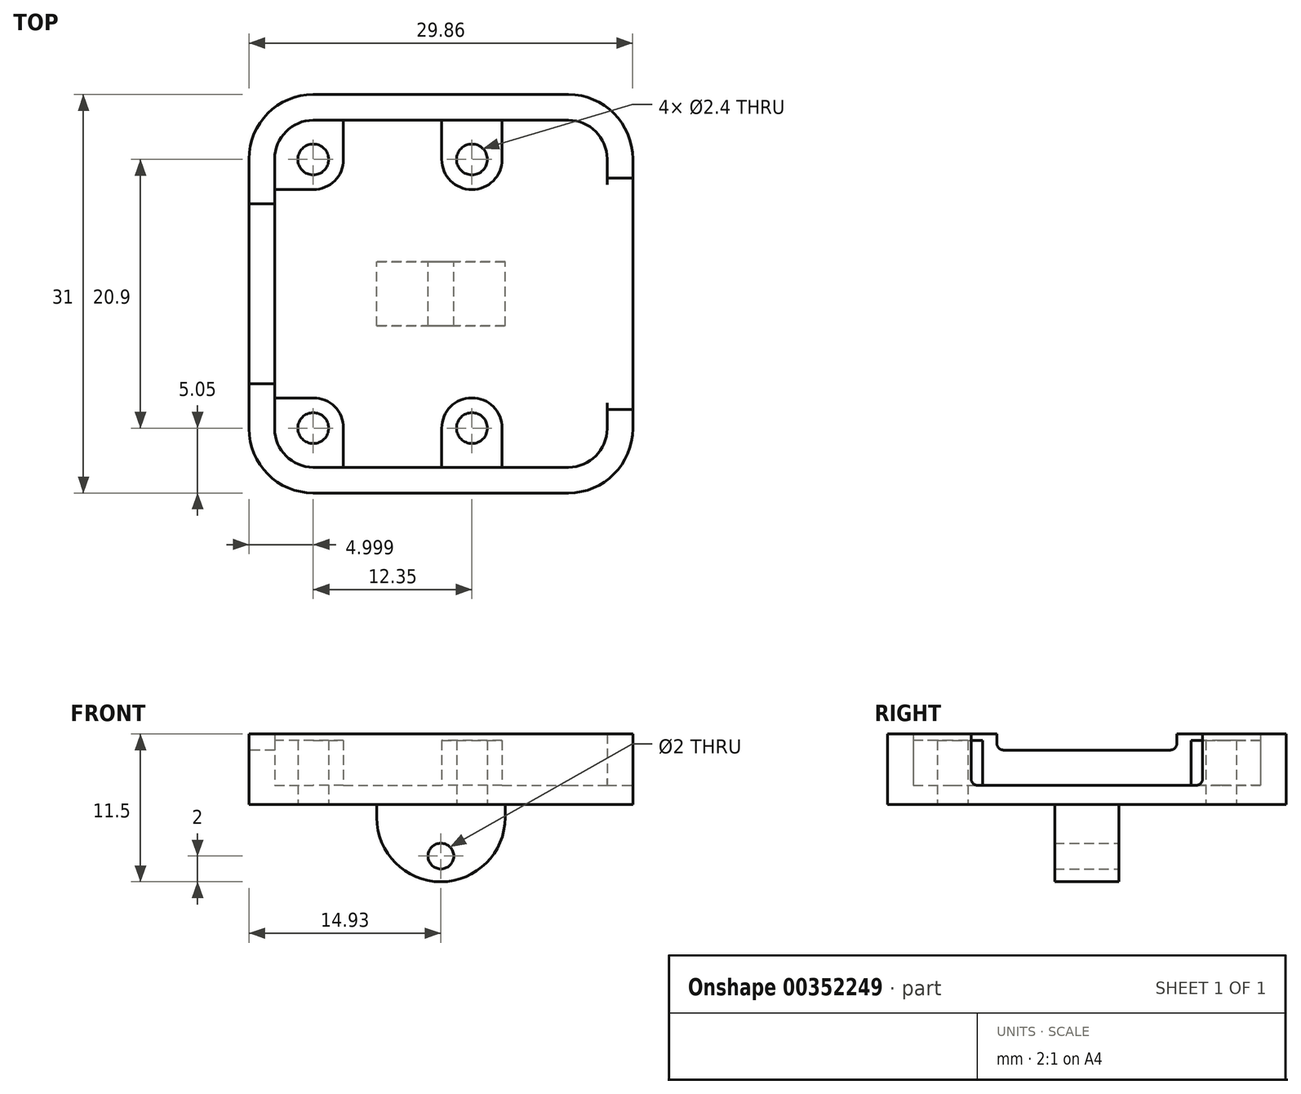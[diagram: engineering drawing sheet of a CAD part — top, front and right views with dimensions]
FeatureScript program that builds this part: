
annotation { "Feature Type Name" : "Feature", "Feature Type Description" : "" }
export const myFeature = defineFeature(function(context is Context, id is Id, definition is map)
    precondition{}
    {
        {
            var Q0;
            Q0=qCreatedBy(makeId("Top.planeOp"),FACE);
            var sketch = newSketch(context, id + "F0", { "sketchPlane" : qUnion([Q0])});
            skPoint(sketch, "E0.middle", {"position": v(0, 0) * mm});
            skPoint(sketch, "E1.visualSharp", {"position": v(-11.93, 12.5) * mm});
            skPoint(sketch, "E2.visualSharp", {"position": v(-11.93, -12.5) * mm});
            skPoint(sketch, "E3.visualSharp", {"position": v(11.93, 12.5) * mm});
            skPoint(sketch, "E4.visualSharp", {"position": v(11.93, -12.5) * mm});
            skLineSegment(sketch, "E5", {"start": v(-9.93, 14.98) * mm, "end": v(-9.93, -15.05) * mm, "construction": true});
            skLineSegment(sketch, "E6", {"start": v(-20.4, -10.45) * mm, "end": v(21.47, -10.45) * mm, "construction": true});
            skLineSegment(sketch, "E7", {"start": v(-14.71, 10.45) * mm, "end": v(19.25, 10.45) * mm, "construction": true});
            skCircle(sketch, "E8", {"center": v(-9.93, 10.45) * mm, "radius": 1.2 * mm});
            skCircle(sketch, "E9", {"center": v(-9.93, -10.45) * mm, "radius": 1.2 * mm});
            skLineSegment(sketch, "E10", {"start": v(2.42, 14.76) * mm, "end": v(2.42, -15.1) * mm, "construction": true});
            skCircle(sketch, "E11", {"center": v(2.42, 10.45) * mm, "radius": 1.2 * mm});
            skCircle(sketch, "E12", {"center": v(2.42, -10.45) * mm, "radius": 1.2 * mm});
            skLineSegment(sketch, "E13", {"start": v(2.47, 15.16) * mm, "end": v(2.47, -14.75) * mm, "construction": true});
            skPoint(sketch, "E14.middle", {"position": v(2.47, 0) * mm});
            skCircle(sketch, "E15", {"center": v(-9.93, 10.45) * mm, "radius": 2.35 * mm});
            skCircle(sketch, "E16", {"center": v(-9.93, -10.45) * mm, "radius": 2.35 * mm});
            skCircle(sketch, "E17", {"center": v(2.42, -10.45) * mm, "radius": 2.35 * mm});
            skCircle(sketch, "E18", {"center": v(2.42, 10.45) * mm, "radius": 2.35 * mm});
            skLineSegment(sketch, "E19.0", {"start": v(9.93, 13.5) * mm, "end": v(-9.93, 13.5) * mm});
            skArc(sketch, "E19.1", {"start": v(12.93, 10.5) * mm, "mid": v(12.05, 12.62) * mm, "end": v(9.93, 13.5) * mm});
            skArc(sketch, "E19.2", {"start": v(-9.93, 13.5) * mm, "mid": v(-12.05, 12.62) * mm, "end": v(-12.93, 10.5) * mm});
            skLineSegment(sketch, "E19.3", {"start": v(12.93, 10.5) * mm, "end": v(12.93, -10.5) * mm});
            skLineSegment(sketch, "E19.4", {"start": v(-12.93, 10.5) * mm, "end": v(-12.93, -10.5) * mm});
            skArc(sketch, "E19.5", {"start": v(-12.93, -10.5) * mm, "mid": v(-12.05, -12.62) * mm, "end": v(-9.93, -13.5) * mm});
            skLineSegment(sketch, "E19.6", {"start": v(9.93, -13.5) * mm, "end": v(-9.93, -13.5) * mm});
            skArc(sketch, "E19.7", {"start": v(9.93, -13.5) * mm, "mid": v(12.05, -12.62) * mm, "end": v(12.93, -10.5) * mm});
            skArc(sketch, "E20.0", {"start": v(14.93, 10.5) * mm, "mid": v(13.47, 14.04) * mm, "end": v(9.93, 15.5) * mm});
            skLineSegment(sketch, "E20.1", {"start": v(14.93, 10.5) * mm, "end": v(14.93, -10.5) * mm});
            skLineSegment(sketch, "E20.2", {"start": v(9.93, 15.5) * mm, "end": v(-9.93, 15.5) * mm});
            skArc(sketch, "E20.3", {"start": v(9.93, -15.5) * mm, "mid": v(13.47, -14.04) * mm, "end": v(14.93, -10.5) * mm});
            skArc(sketch, "E20.4", {"start": v(-9.93, 15.5) * mm, "mid": v(-13.47, 14.04) * mm, "end": v(-14.93, 10.5) * mm});
            skLineSegment(sketch, "E20.5", {"start": v(-14.93, 10.5) * mm, "end": v(-14.93, -10.5) * mm});
            skArc(sketch, "E20.6", {"start": v(-14.93, -10.5) * mm, "mid": v(-13.47, -14.04) * mm, "end": v(-9.93, -15.5) * mm});
            skLineSegment(sketch, "E20.7", {"start": v(9.93, -15.5) * mm, "end": v(-9.93, -15.5) * mm});
            skLineSegment(sketch, "E21", {"start": v(-9.93, 8.1) * mm, "end": v(-12.93, 8.1) * mm});
            skLineSegment(sketch, "E22", {"start": v(-7.58, 10.45) * mm, "end": v(-7.58, 13.5) * mm});
            skLineSegment(sketch, "E23", {"start": v(0.07, 10.45) * mm, "end": v(0.07, 13.5) * mm});
            skLineSegment(sketch, "E24", {"start": v(4.77, 10.45) * mm, "end": v(4.77, 13.5) * mm});
            skLineSegment(sketch, "E25", {"start": v(0.07, -10.45) * mm, "end": v(0.07, -13.5) * mm});
            skLineSegment(sketch, "E26", {"start": v(4.77, -10.45) * mm, "end": v(4.77, -13.5) * mm});
            skLineSegment(sketch, "E27", {"start": v(-9.93, -8.1) * mm, "end": v(-12.93, -8.1) * mm});
            skLineSegment(sketch, "E28", {"start": v(-7.58, -10.45) * mm, "end": v(-7.58, -13.5) * mm});
            skSolve(sketch);
        }
        {
            var Q0;
            Q0=makeQuery(id+"F0.imprint","IMPRINT",FACE,{"disambiguationData":[TD([[makeQuery(id+"F0.imprint","IMPRINT",EDGE,{"derivedFrom":sQuery(id+"F0.wireOp",EDGE,"E19.0")}),-1.0]])]});
            var Q1;
            Q1=makeQuery(id+"F0.imprint","IMPRINT",FACE,{"disambiguationData":[TD([[makeQuery(id+"F0.imprint","IMPRINT",EDGE,{"derivedFrom":sQuery(id+"F0.wireOp",EDGE,"E0.left")}),-1.0]])]});
            var Q2;
            Q2=makeQuery(id+"F0.imprint","IMPRINT",FACE,{"disambiguationData":[TD([[makeQuery(id+"F0.imprint","IMPRINT",EDGE,{"derivedFrom":sQuery(id+"F0.wireOp",EDGE,"E12")}),-1.0]])]});
            var Q3;
            {var subQ0=sQuery(id+"F0.wireOp",EDGE,"E2.filletArc");Q3=makeQuery(id+"F0.imprint","IMPRINT",FACE,{"disambiguationData":[TD([[makeQuery(id+"F0.imprint","IMPRINT",EDGE,{"derivedFrom":subQ0}),1.0]])]});}
            var Q4;
            Q4=makeQuery(id+"F0.imprint","IMPRINT",FACE,{"disambiguationData":[TD([[makeQuery(id+"F0.imprint","IMPRINT",EDGE,{"derivedFrom":sQuery(id+"F0.wireOp",EDGE,"E0.left")}),1.0]])]});
            var Q5;
            {var subQ0=sQuery(id+"F0.wireOp",EDGE,"E1.filletArc");Q5=makeQuery(id+"F0.imprint","IMPRINT",FACE,{"disambiguationData":[TD([[makeQuery(id+"F0.imprint","IMPRINT",EDGE,{"derivedFrom":subQ0}),1.0]])]});}
            var Q6;
            Q6=makeQuery(id+"F0.imprint","IMPRINT",FACE,{"disambiguationData":[TD([[makeQuery(id+"F0.imprint","IMPRINT",EDGE,{"derivedFrom":sQuery(id+"F0.wireOp",EDGE,"E11")}),-1.0]])]});
            var Q7;
            {var subQ0=sQuery(id+"F0.wireOp",EDGE,"E18");var subQ1=sQuery(id+"F0.wireOp",EDGE,"E0.bottom");var subQ2=makeQuery(id+"F0.imprint","INTERSECT",VERTEX,{"disambiguationData":[OD(0.0)],"derivedFrom":[subQ1,subQ0]});Q7=makeQuery(id+"F0.imprint","IMPRINT",FACE,{"disambiguationData":[TD([[makeQuery(id+"F0.imprint","IMPRINT",EDGE,{"disambiguationData":[TD([[subQ2,-1.0]])],"derivedFrom":subQ1}),-1.0]])]});}
            var Q8;
            {var subQ0=sQuery(id+"F0.wireOp",EDGE,"E1.filletArc");Q8=makeQuery(id+"F0.imprint","IMPRINT",FACE,{"disambiguationData":[TD([[makeQuery(id+"F0.imprint","IMPRINT",EDGE,{"derivedFrom":subQ0}),-1.0]])]});}
            var Q9;
            {var subQ0=sQuery(id+"F0.wireOp",EDGE,"E2.filletArc");Q9=makeQuery(id+"F0.imprint","IMPRINT",FACE,{"disambiguationData":[TD([[makeQuery(id+"F0.imprint","IMPRINT",EDGE,{"derivedFrom":subQ0}),-1.0]])]});}
            var Q10;
            {var subQ0=sQuery(id+"F0.wireOp",EDGE,"E17");var subQ1=sQuery(id+"F0.wireOp",EDGE,"E0.top");var subQ2=makeQuery(id+"F0.imprint","INTERSECT",VERTEX,{"disambiguationData":[OD(0.0)],"derivedFrom":[subQ1,subQ0]});Q10=makeQuery(id+"F0.imprint","IMPRINT",FACE,{"disambiguationData":[TD([[makeQuery(id+"F0.imprint","IMPRINT",EDGE,{"disambiguationData":[TD([[subQ2,-1.0]])],"derivedFrom":subQ1}),1.0]])]});}
            var Q11;
            {var subQ0=sQuery(id+"F0.wireOp",EDGE,"E19.2");Q11=makeQuery(id+"F0.imprint","IMPRINT",FACE,{"disambiguationData":[TD([[makeQuery(id+"F0.imprint","IMPRINT",EDGE,{"derivedFrom":subQ0}),1.0]])]});}
            var Q12;
            {var subQ0=sQuery(id+"F0.wireOp",EDGE,"E21");var subQ1=sQuery(id+"F0.wireOp",EDGE,"E0.right");var subQ2=makeQuery(id+"F0.imprint","INTERSECT",VERTEX,{"derivedFrom":[subQ1,subQ0]});Q12=makeQuery(id+"F0.imprint","IMPRINT",FACE,{"disambiguationData":[TD([[makeQuery(id+"F0.imprint","IMPRINT",EDGE,{"disambiguationData":[TD([[subQ2,-1.0]])],"derivedFrom":subQ1}),-1.0]])]});}
            var Q13;
            {var subQ0=sQuery(id+"F0.wireOp",EDGE,"E19.5");Q13=makeQuery(id+"F0.imprint","IMPRINT",FACE,{"disambiguationData":[TD([[makeQuery(id+"F0.imprint","IMPRINT",EDGE,{"derivedFrom":subQ0}),1.0]])]});}
            var Q14;
            {var subQ0=sQuery(id+"F0.wireOp",EDGE,"E27");var subQ1=sQuery(id+"F0.wireOp",EDGE,"E0.right");var subQ2=makeQuery(id+"F0.imprint","INTERSECT",VERTEX,{"derivedFrom":[subQ1,subQ0]});Q14=makeQuery(id+"F0.imprint","IMPRINT",FACE,{"disambiguationData":[TD([[makeQuery(id+"F0.imprint","IMPRINT",EDGE,{"disambiguationData":[TD([[subQ2,-1.0]])],"derivedFrom":subQ1}),1.0]])]});}
            var Q15;
            {var subQ0=sQuery(id+"F0.wireOp",EDGE,"E28");var subQ1=sQuery(id+"F0.wireOp",EDGE,"E0.top");var subQ2=makeQuery(id+"F0.imprint","INTERSECT",VERTEX,{"derivedFrom":[subQ1,subQ0]});Q15=makeQuery(id+"F0.imprint","IMPRINT",FACE,{"disambiguationData":[TD([[makeQuery(id+"F0.imprint","IMPRINT",EDGE,{"disambiguationData":[TD([[subQ2,-1.0]])],"derivedFrom":subQ1}),-1.0]])]});}
            var Q16;
            {var subQ0=sQuery(id+"F0.wireOp",EDGE,"E25");var subQ1=sQuery(id+"F0.wireOp",EDGE,"E0.top");var subQ2=makeQuery(id+"F0.imprint","INTERSECT",VERTEX,{"derivedFrom":[subQ1,subQ0]});Q16=makeQuery(id+"F0.imprint","IMPRINT",FACE,{"disambiguationData":[TD([[makeQuery(id+"F0.imprint","IMPRINT",EDGE,{"disambiguationData":[TD([[subQ2,-1.0]])],"derivedFrom":subQ1}),1.0]])]});}
            var Q17;
            {var subQ3=sQuery(id+"F0.wireOp",EDGE,"E26");var subQ6=sQuery(id+"F0.wireOp",EDGE,"E0.top");var subQ10=makeQuery(id+"F0.imprint","INTERSECT",VERTEX,{"derivedFrom":[subQ6,subQ3]});Q17=makeQuery(id+"F0.imprint","IMPRINT",FACE,{"disambiguationData":[TD([[makeQuery(id+"F0.imprint","IMPRINT",EDGE,{"disambiguationData":[TD([[subQ10,-1.0]])],"derivedFrom":subQ6}),1.0]])]});}
            var Q18;
            {var subQ0=sQuery(id+"F0.wireOp",EDGE,"E26");var subQ1=sQuery(id+"F0.wireOp",EDGE,"E0.top");var subQ2=makeQuery(id+"F0.imprint","INTERSECT",VERTEX,{"derivedFrom":[subQ1,subQ0]});Q18=makeQuery(id+"F0.imprint","IMPRINT",FACE,{"disambiguationData":[TD([[makeQuery(id+"F0.imprint","IMPRINT",EDGE,{"disambiguationData":[TD([[subQ2,-1.0]])],"derivedFrom":subQ1}),-1.0]])]});}
            var Q19;
            {var subQ0=sQuery(id+"F0.wireOp",EDGE,"E17");var subQ1=sQuery(id+"F0.wireOp",EDGE,"E0.top");var subQ2=makeQuery(id+"F0.imprint","INTERSECT",VERTEX,{"disambiguationData":[OD(1.0)],"derivedFrom":[subQ1,subQ0]});Q19=makeQuery(id+"F0.imprint","IMPRINT",FACE,{"disambiguationData":[TD([[makeQuery(id+"F0.imprint","IMPRINT",EDGE,{"disambiguationData":[TD([[subQ2,-1.0]])],"derivedFrom":subQ1}),-1.0]])]});}
            var Q20;
            {var subQ0=sQuery(id+"F0.wireOp",EDGE,"E22");var subQ1=sQuery(id+"F0.wireOp",EDGE,"E0.bottom");var subQ2=makeQuery(id+"F0.imprint","INTERSECT",VERTEX,{"derivedFrom":[subQ1,subQ0]});Q20=makeQuery(id+"F0.imprint","IMPRINT",FACE,{"disambiguationData":[TD([[makeQuery(id+"F0.imprint","IMPRINT",EDGE,{"disambiguationData":[TD([[subQ2,-1.0]])],"derivedFrom":subQ1}),1.0]])]});}
            var Q21;
            {var subQ0=sQuery(id+"F0.wireOp",EDGE,"E15");var subQ1=sQuery(id+"F0.wireOp",EDGE,"E0.right");var subQ2=makeQuery(id+"F0.imprint","INTERSECT",VERTEX,{"derivedFrom":[subQ1,subQ0]});Q21=makeQuery(id+"F0.imprint","IMPRINT",FACE,{"disambiguationData":[TD([[makeQuery(id+"F0.imprint","IMPRINT",EDGE,{"disambiguationData":[TD([[subQ2,-1.0]])],"derivedFrom":subQ1}),1.0]])]});}
            var Q22;
            {var subQ0=sQuery(id+"F0.wireOp",EDGE,"E23");var subQ1=sQuery(id+"F0.wireOp",EDGE,"E0.bottom");var subQ2=makeQuery(id+"F0.imprint","INTERSECT",VERTEX,{"derivedFrom":[subQ1,subQ0]});Q22=makeQuery(id+"F0.imprint","IMPRINT",FACE,{"disambiguationData":[TD([[makeQuery(id+"F0.imprint","IMPRINT",EDGE,{"disambiguationData":[TD([[subQ2,-1.0]])],"derivedFrom":subQ1}),-1.0]])]});}
            var Q23;
            {var subQ0=sQuery(id+"F0.wireOp",EDGE,"E18");var subQ1=sQuery(id+"F0.wireOp",EDGE,"E0.bottom");var subQ2=makeQuery(id+"F0.imprint","INTERSECT",VERTEX,{"disambiguationData":[OD(1.0)],"derivedFrom":[subQ1,subQ0]});Q23=makeQuery(id+"F0.imprint","IMPRINT",FACE,{"disambiguationData":[TD([[makeQuery(id+"F0.imprint","IMPRINT",EDGE,{"disambiguationData":[TD([[subQ2,-1.0]])],"derivedFrom":subQ1}),1.0]])]});}
            var Q24;
            {var subQ1=sQuery(id+"F0.wireOp",EDGE,"E0.bottom");var subQ7=sQuery(id+"F0.wireOp",EDGE,"E24");var subQ9=makeQuery(id+"F0.imprint","INTERSECT",VERTEX,{"derivedFrom":[subQ1,subQ7]});Q24=makeQuery(id+"F0.imprint","IMPRINT",FACE,{"disambiguationData":[TD([[makeQuery(id+"F0.imprint","IMPRINT",EDGE,{"disambiguationData":[TD([[subQ9,-1.0]])],"derivedFrom":subQ1}),-1.0]])]});}
            var Q25;
            {var subQ0=sQuery(id+"F0.wireOp",EDGE,"E24");var subQ1=sQuery(id+"F0.wireOp",EDGE,"E0.bottom");var subQ2=makeQuery(id+"F0.imprint","INTERSECT",VERTEX,{"derivedFrom":[subQ1,subQ0]});Q25=makeQuery(id+"F0.imprint","IMPRINT",FACE,{"disambiguationData":[TD([[makeQuery(id+"F0.imprint","IMPRINT",EDGE,{"disambiguationData":[TD([[subQ2,-1.0]])],"derivedFrom":subQ1}),1.0]])]});}
            var Q26;
            Q26=makeQuery(id+"F0.imprint","IMPRINT",FACE,{"disambiguationData":[TD([[makeQuery(id+"F0.imprint","IMPRINT",EDGE,{"derivedFrom":sQuery(id+"F0.wireOp",EDGE,"0e7cc196-94d9-4211-9143-2209eafa79fa.0")}),-1.0]])]});
            var Q27;
            Q27=makeQuery(id+"F0.imprint","IMPRINT",FACE,{"disambiguationData":[TD([[makeQuery(id+"F0.imprint","IMPRINT",EDGE,{"derivedFrom":sQuery(id+"F0.wireOp",EDGE,"E9")}),-1.0]])]});
            var Q28;
            {var subQ0=sQuery(id+"F0.wireOp",EDGE,"E25");Q28=makeQuery(id+"F0.imprint","IMPRINT",FACE,{"disambiguationData":[TD([[makeQuery(id+"F0.imprint","IMPRINT",EDGE,{"derivedFrom":subQ0}),1.0]])]});}
            var Q29;
            Q29=makeQuery(id+"F0.imprint","IMPRINT",FACE,{"disambiguationData":[TD([[makeQuery(id+"F0.imprint","IMPRINT",EDGE,{"derivedFrom":sQuery(id+"F0.wireOp",EDGE,"E8")}),-1.0]])]});
            var Q30;
            {var subQ0=sQuery(id+"F0.wireOp",EDGE,"E23");Q30=makeQuery(id+"F0.imprint","IMPRINT",FACE,{"disambiguationData":[TD([[makeQuery(id+"F0.imprint","IMPRINT",EDGE,{"derivedFrom":subQ0}),-1.0]])]});}
            var Q31;
            {var subQ13=sQuery(id+"F0.wireOp",EDGE,"E19.1");Q31=makeQuery(id+"F0.imprint","IMPRINT",FACE,{"disambiguationData":[TD([[makeQuery(id+"F0.imprint","IMPRINT",EDGE,{"derivedFrom":subQ13}),1.0]])]});}
            extrude(context, id + "F1", {"entities" : qUnion([Q0, Q1, Q2, Q3, Q4, Q5, Q6, Q7, Q8, Q9, Q10, Q11, Q12, Q13, Q14, Q15, Q16, Q17, Q18, Q19, Q20, Q21, Q22, Q23, Q24, Q25, Q26, Q27, Q28, Q29, Q30, Q31]), "depth" : 1.5 * mm});
        }
        {
            var Q0;
            {var subQ1=sQuery(id+"F0.wireOp",EDGE,"E19.2");Q0=makeQuery(id+"F0.imprint","IMPRINT",FACE,{"disambiguationData":[TD([[makeQuery(id+"F0.imprint","IMPRINT",EDGE,{"derivedFrom":subQ1}),1.0]])]});}
            var Q1;
            Q1=makeQuery(id+"F0.imprint","IMPRINT",FACE,{"disambiguationData":[TD([[makeQuery(id+"F0.imprint","IMPRINT",EDGE,{"derivedFrom":sQuery(id+"F0.wireOp",EDGE,"E8")}),-1.0]])]});
            var Q2;
            Q2=makeQuery(id+"F0.imprint","IMPRINT",FACE,{"disambiguationData":[TD([[makeQuery(id+"F0.imprint","IMPRINT",EDGE,{"derivedFrom":sQuery(id+"F0.wireOp",EDGE,"E11")}),-1.0]])]});
            var Q3;
            {var subQ0=sQuery(id+"F0.wireOp",EDGE,"E23");Q3=makeQuery(id+"F0.imprint","IMPRINT",FACE,{"disambiguationData":[TD([[makeQuery(id+"F0.imprint","IMPRINT",EDGE,{"derivedFrom":subQ0}),-1.0]])]});}
            var Q4;
            Q4=makeQuery(id+"F0.imprint","IMPRINT",FACE,{"disambiguationData":[TD([[makeQuery(id+"F0.imprint","IMPRINT",EDGE,{"derivedFrom":sQuery(id+"F0.wireOp",EDGE,"E12")}),-1.0]])]});
            var Q5;
            {var subQ0=sQuery(id+"F0.wireOp",EDGE,"E25");Q5=makeQuery(id+"F0.imprint","IMPRINT",FACE,{"disambiguationData":[TD([[makeQuery(id+"F0.imprint","IMPRINT",EDGE,{"derivedFrom":subQ0}),1.0]])]});}
            var Q6;
            Q6=makeQuery(id+"F0.imprint","IMPRINT",FACE,{"disambiguationData":[TD([[makeQuery(id+"F0.imprint","IMPRINT",EDGE,{"derivedFrom":sQuery(id+"F0.wireOp",EDGE,"E9")}),-1.0]])]});
            var Q7;
            {var subQ1=sQuery(id+"F0.wireOp",EDGE,"E19.5");Q7=makeQuery(id+"F0.imprint","IMPRINT",FACE,{"disambiguationData":[TD([[makeQuery(id+"F0.imprint","IMPRINT",EDGE,{"derivedFrom":subQ1}),1.0]])]});}
            extrude(context, id + "F2", {"entities" : qUnion([Q0, Q1, Q2, Q3, Q4, Q5, Q6, Q7]), "operationType" : NewBodyOperationType.ADD, "depth" : 5 * mm});
        }
        {
            var Q0;
            {var subQ12=sQuery(id+"F0.wireOp",EDGE,"E19.1");Q0=makeQuery(id+"F0.imprint","IMPRINT",FACE,{"disambiguationData":[TD([[makeQuery(id+"F0.imprint","IMPRINT",EDGE,{"derivedFrom":subQ12}),-1.0]])]});}
            extrude(context, id + "F3", {"entities" : qUnion([Q0]), "operationType" : NewBodyOperationType.ADD, "depth" : 5.5 * mm});
        }
        {
            var Q0;
            {var subQ0=sQuery(id+"F0.wireOp",EDGE,"E20.5");Q0=makeQuery(id+"F3.boolean.opBoolean","MERGE",FACE,{"derivedFrom":[makeQuery(id+"F1.opExtrude","SWEPT_FACE",FACE,{"disambiguationData":[OSD([subQ0])]}),makeQuery(id+"F3.opExtrude","SWEPT_FACE",FACE,{"disambiguationData":[OSD([subQ0])]})]});}
            var sketch = newSketch(context, id + "F4", { "sketchPlane" : qUnion([Q0])});
            skLineSegment(sketch, "E29.bottom", {"start": v(-7, 5.5) * mm, "end": v(7, 5.5) * mm});
            skLineSegment(sketch, "E29.top", {"start": v(-6.5, 4.25) * mm, "end": v(6.5, 4.25) * mm});
            skLineSegment(sketch, "E29.left", {"start": v(-7, 5.5) * mm, "end": v(-7, 4.75) * mm});
            skLineSegment(sketch, "E29.right", {"start": v(7, 5.5) * mm, "end": v(7, 4.75) * mm});
            skPoint(sketch, "E30.visualSharp", {"position": v(-7, 4.25) * mm});
            skArc(sketch, "E30.filletArc", {"start": v(-7, 4.75) * mm, "mid": v(-6.85, 4.4) * mm, "end": v(-6.5, 4.25) * mm});
            skPoint(sketch, "E31.visualSharp", {"position": v(7, 4.25) * mm});
            skArc(sketch, "E31.filletArc", {"start": v(6.5, 4.25) * mm, "mid": v(6.85, 4.4) * mm, "end": v(7, 4.75) * mm});
            skSolve(sketch);
        }
        {
            var Q0;
            Q0=makeQuery(id+"F4.imprint","IMPRINT",FACE,{"disambiguationData":[TD([[makeQuery(id+"F4.imprint","IMPRINT",EDGE,{"derivedFrom":sQuery(id+"F4.wireOp",EDGE,"E29.bottom")}),-1.0]])]});
            extrude(context, id + "F5", {"entities" : qUnion([Q0]), "operationType" : NewBodyOperationType.REMOVE, "oppositeDirection" : true, "depth" : 2 * mm});
        }
        {
            var Q0;
            {var subQ0=sQuery(id+"F0.wireOp",EDGE,"E20.1");Q0=makeQuery(id+"F3.boolean.opBoolean","MERGE",FACE,{"derivedFrom":[makeQuery(id+"F1.opExtrude","SWEPT_FACE",FACE,{"disambiguationData":[OSD([subQ0])]}),makeQuery(id+"F3.opExtrude","SWEPT_FACE",FACE,{"disambiguationData":[OSD([subQ0])]})]});}
            var sketch = newSketch(context, id + "F6", { "sketchPlane" : qUnion([Q0])});
            skLineSegment(sketch, "E32.bottom", {"start": v(9, 5.5) * mm, "end": v(-9, 5.5) * mm});
            skLineSegment(sketch, "E32.top", {"start": v(8.5, 1.5) * mm, "end": v(-8.5, 1.5) * mm});
            skLineSegment(sketch, "E32.left", {"start": v(9, 5.5) * mm, "end": v(9, 2) * mm});
            skLineSegment(sketch, "E32.right", {"start": v(-9, 5.5) * mm, "end": v(-9, 2) * mm});
            skPoint(sketch, "E32.middle", {"position": v(0, 3.5) * mm});
            skPoint(sketch, "E33.visualSharp", {"position": v(-9, 1.5) * mm});
            skArc(sketch, "E33.filletArc", {"start": v(-9, 2) * mm, "mid": v(-8.85, 1.65) * mm, "end": v(-8.5, 1.5) * mm});
            skPoint(sketch, "E34.visualSharp", {"position": v(9, 1.5) * mm});
            skArc(sketch, "E34.filletArc", {"start": v(8.5, 1.5) * mm, "mid": v(8.85, 1.65) * mm, "end": v(9, 2) * mm});
            skSolve(sketch);
        }
        {
            var Q0;
            Q0=makeQuery(id+"F6.imprint","IMPRINT",FACE,{"disambiguationData":[TD([[makeQuery(id+"F6.imprint","IMPRINT",EDGE,{"derivedFrom":sQuery(id+"F6.wireOp",EDGE,"E32.bottom")}),1.0]])]});
            extrude(context, id + "F7", {"entities" : qUnion([Q0]), "operationType" : NewBodyOperationType.REMOVE, "oppositeDirection" : true, "depth" : 2 * mm});
        }
        {
            var Q0;
            {var subQ10=sQuery(id+"F0.wireOp",EDGE,"E19.1");Q0=makeQuery(id+"F0.imprint","IMPRINT",FACE,{"disambiguationData":[TD([[makeQuery(id+"F0.imprint","IMPRINT",EDGE,{"derivedFrom":subQ10}),1.0]])]});}
            var sketch = newSketch(context, id + "F8", { "sketchPlane" : qUnion([Q0])});
            skLineSegment(sketch, "E35.bottom", {"start": v(-5, -2.5) * mm, "end": v(5, -2.5) * mm});
            skLineSegment(sketch, "E35.top", {"start": v(-5, 2.5) * mm, "end": v(5, 2.5) * mm});
            skLineSegment(sketch, "E35.left", {"start": v(-5, -2.5) * mm, "end": v(-5, 2.5) * mm});
            skLineSegment(sketch, "E35.right", {"start": v(5, -2.5) * mm, "end": v(5, 2.5) * mm});
            skPoint(sketch, "E35.middle", {"position": v(0, 0) * mm});
            skSolve(sketch);
        }
        {
            var Q0;
            Q0 = qSketchRegion(id + "F8", true);
            extrude(context, id + "F9", {"entities" : qUnion([Q0]), "operationType" : NewBodyOperationType.ADD, "oppositeDirection" : true, "depth" : 1 * mm, "offsetDistance" : 25 * mm});
        }
        {
            var Q0;
            Q0=makeQuery(id+"F9.opExtrude","SWEPT_FACE",FACE,{"disambiguationData":[OSD([sQuery(id+"F8.wireOp",EDGE,"E35.top")])]});
            var sketch = newSketch(context, id + "F10", { "sketchPlane" : qUnion([Q0])});
            skArc(sketch, "E36", {"start": v(-5, -1) * mm, "mid": v(0, -6) * mm, "end": v(5, -1) * mm});
            skCircle(sketch, "E37", {"center": v(0, -4) * mm, "radius": 1 * mm});
            skSolve(sketch);
        }
        {
            var Q0;
            Q0=makeQuery(id+"F10.imprint","IMPRINT",FACE,{"disambiguationData":[TD([[makeQuery(id+"F10.imprint","IMPRINT",EDGE,{"derivedFrom":sQuery(id+"F10.wireOp",EDGE,"E36")}),1.0]])]});
            extrude(context, id + "F11", {"entities" : qUnion([Q0]), "operationType" : NewBodyOperationType.ADD, "oppositeDirection" : true, "depth" : 5 * mm, "offsetDistance" : 25 * mm});
        }
    });
